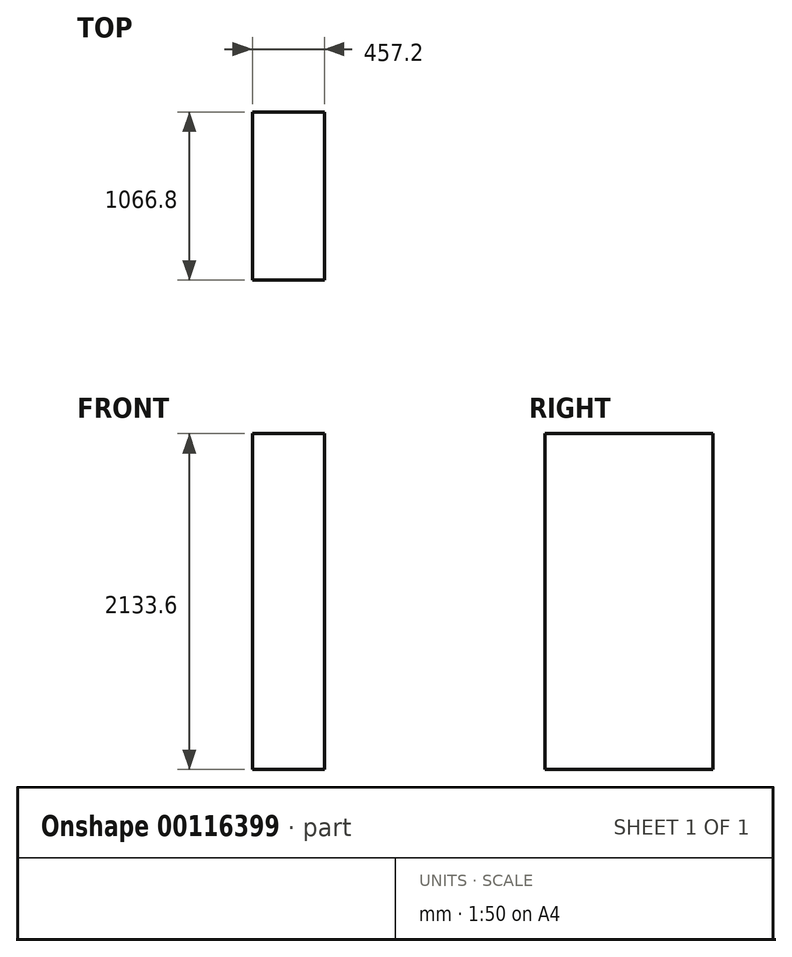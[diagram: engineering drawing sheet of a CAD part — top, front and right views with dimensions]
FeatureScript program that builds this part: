
annotation { "Feature Type Name" : "Feature", "Feature Type Description" : "" }
export const myFeature = defineFeature(function(context is Context, id is Id, definition is map)
    precondition{}
    {
        {
            var Q0;
            Q0=qCreatedBy(makeId("Top.planeOp"),FACE);
            var sketch = newSketch(context, id + "F0", { "sketchPlane" : qUnion([Q0])});
            skLineSegment(sketch, "E0.bottom", {"start": v(123.35, 999.48) * mm, "end": v(-333.85, 999.48) * mm});
            skLineSegment(sketch, "E0.top", {"start": v(123.35, -67.32) * mm, "end": v(-333.85, -67.32) * mm});
            skLineSegment(sketch, "E0.left", {"start": v(123.35, 999.48) * mm, "end": v(123.35, -67.32) * mm});
            skLineSegment(sketch, "E0.right", {"start": v(-333.85, 999.48) * mm, "end": v(-333.85, -67.32) * mm});
            skPoint(sketch, "E0.middle", {"position": v(-105.25, 466.08) * mm});
            skSolve(sketch);
        }
        {
            var Q0;
            Q0=makeQuery(id+"F0.imprint","IMPRINT",FACE,{"disambiguationData":[TD([[makeQuery(id+"F0.imprint","IMPRINT",EDGE,{"derivedFrom":sQuery(id+"F0.wireOp",EDGE,"E0.bottom")}),1.0]])]});
            extrude(context, id + "F1", {"entities" : qUnion([Q0]), "depth" : 2133.6 * mm});
        }
    });
